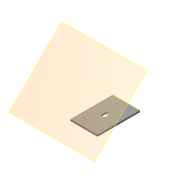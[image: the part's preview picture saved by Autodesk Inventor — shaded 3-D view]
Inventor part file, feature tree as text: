
AUTODESK INVENTOR PART (.ipt)
format: ipt  version: 2019 (Build 230136000, 136)  size: 126,464 bytes
history: native  units: in
note: dims shown in document units (in); Inventor stores cm internally (conversion verified against a paired STEP export)
features: extrude x3, sketch x3, other x3, plane x2, projected_geometry x2
ambient origin geometry x8: Origin, YZ Plane, XZ Plane, XY Plane, X Axis, Y Axis, Z Axis, Center Point
bodies: Solid1 (feature_tree)
feature tree (13):
  extrude  "Extrusion1"  Depth=0.9843in
  plane  "Work Plane1"
  extrude  "Extrusion2"  Depth=0.0127in
  plane  "Work Plane2"
  extrude  "Extrusion3"  Depth=1.0in TaperAngle=0.0deg
  sketch  "Sketch1"  dims[d0=0.6299in d1=0.9843in]
  sketch  "Sketch2"  dims[d2=0.0394in d3=0.0in d4=0.0127in]
  sketch  "Sketch3"  dims[d5=0.0079in d6=0.0in d7=1.0in d8=0.0in]
  projected_geometry  "Projected Loop1"
  projected_geometry  "Projected Loop2"
  other  "Assembly_Cube_Dichroic_Beamsplitter.iam"
  other  "Assembly_Cube_empty_1x1_v2:1"
  other  "10_Cube_1x1_v2:1"
